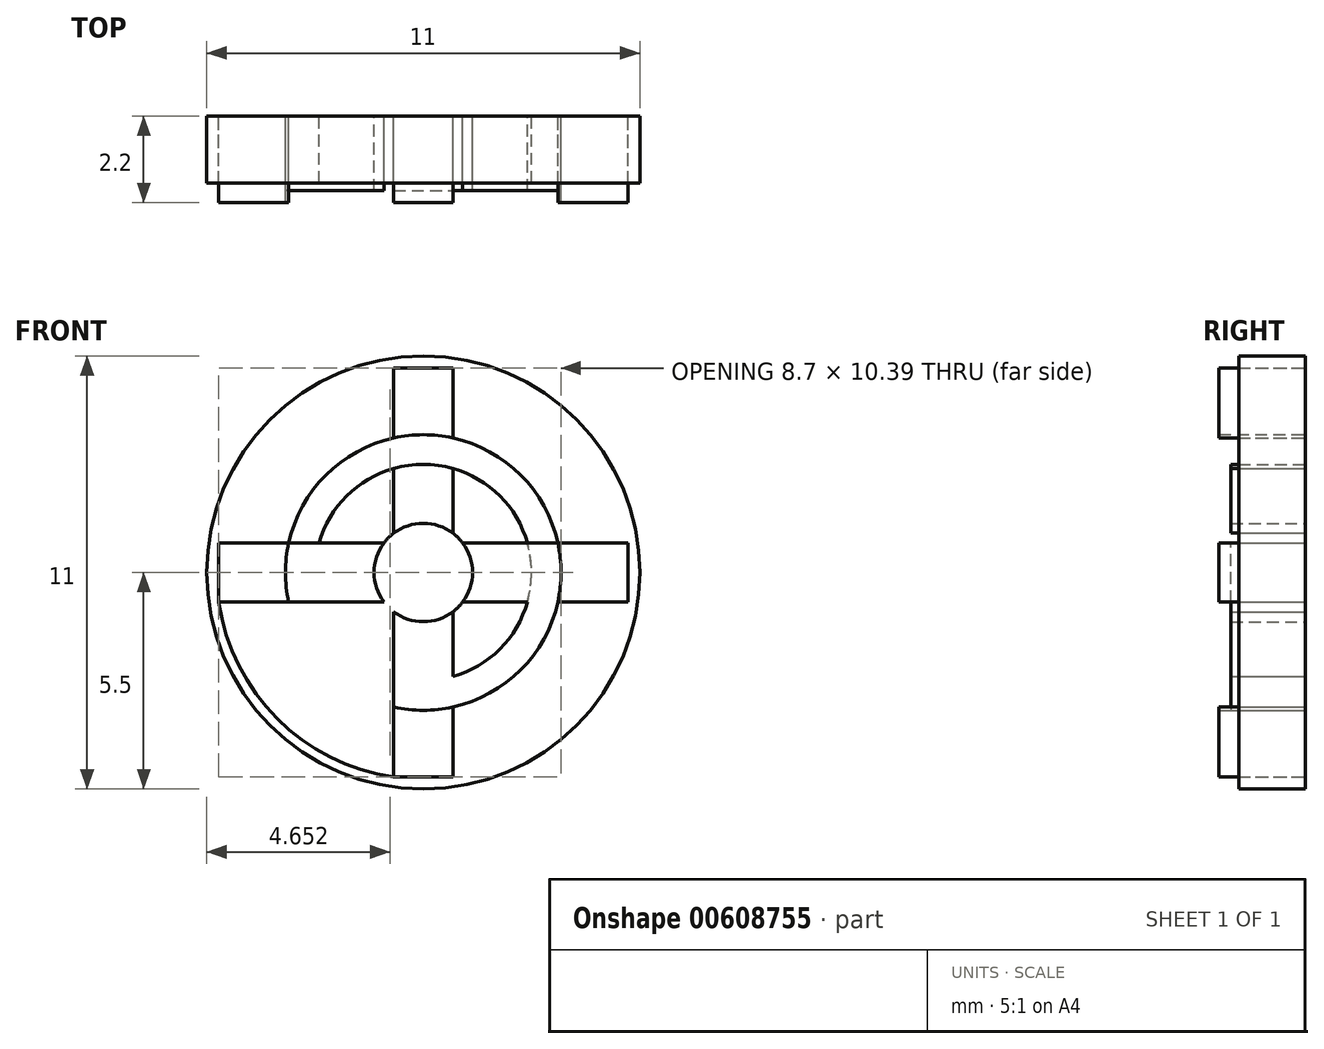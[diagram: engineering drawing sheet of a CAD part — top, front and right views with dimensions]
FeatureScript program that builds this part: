
annotation { "Feature Type Name" : "Feature", "Feature Type Description" : "" }
export const myFeature = defineFeature(function(context is Context, id is Id, definition is map)
    precondition{}
    {
        {
            var Q0;
            Q0=qCreatedBy(makeId("Front.planeOp"),FACE);
            var sketch = newSketch(context, id + "F0", { "sketchPlane" : qUnion([Q0])});
            skCircle(sketch, "E0", {"center": v(0, 0) * mm, "radius": 5.5 * mm});
            skCircle(sketch, "E1", {"center": v(0, 0) * mm, "radius": 1.25 * mm});
            skCircle(sketch, "E2", {"center": v(0, 0) * mm, "radius": 2.75 * mm});
            skCircle(sketch, "E3", {"center": v(0, 0) * mm, "radius": 3.5 * mm});
            skCircle(sketch, "E4", {"center": v(0, 0) * mm, "radius": 5.25 * mm});
            skLineSegment(sketch, "E5.bottom", {"start": v(-5.2, -0.75) * mm, "end": v(5.2, -0.75) * mm});
            skLineSegment(sketch, "E5.top", {"start": v(-5.2, 0.75) * mm, "end": v(5.2, 0.75) * mm});
            skLineSegment(sketch, "E5.left", {"start": v(-5.2, -0.75) * mm, "end": v(-5.2, 0.75) * mm});
            skLineSegment(sketch, "E5.right", {"start": v(5.2, -0.75) * mm, "end": v(5.2, 0.75) * mm});
            skLineSegment(sketch, "E6.bottom", {"start": v(-0.75, -5.2) * mm, "end": v(0.75, -5.2) * mm});
            skLineSegment(sketch, "E6.top", {"start": v(-0.75, 5.2) * mm, "end": v(0.75, 5.2) * mm});
            skLineSegment(sketch, "E6.left", {"start": v(-0.75, -5.2) * mm, "end": v(-0.75, 5.2) * mm});
            skLineSegment(sketch, "E6.right", {"start": v(0.75, -5.2) * mm, "end": v(0.75, 5.2) * mm});
            skSolve(sketch);
        }
        {
            var Q0;
            {var subQ0=sQuery(id+"F0.wireOp",EDGE,"E6.right");var subQ1=sQuery(id+"F0.wireOp",EDGE,"E1");var subQ2=makeQuery(id+"F0.imprint","INTERSECT",VERTEX,{"disambiguationData":[OD(0.0)],"derivedFrom":[subQ1,subQ0]});Q0=makeQuery(id+"F0.imprint","IMPRINT",FACE,{"disambiguationData":[TD([[makeQuery(id+"F0.imprint","IMPRINT",EDGE,{"disambiguationData":[TD([[subQ2,1.0]])],"derivedFrom":subQ1}),-1.0]])]});}
            var Q1;
            {var subQ0=sQuery(id+"F0.wireOp",EDGE,"E6.right");var subQ1=sQuery(id+"F0.wireOp",EDGE,"E3");var subQ2=makeQuery(id+"F0.imprint","INTERSECT",VERTEX,{"disambiguationData":[OD(0.0)],"derivedFrom":[subQ1,subQ0]});Q1=makeQuery(id+"F0.imprint","IMPRINT",FACE,{"disambiguationData":[TD([[makeQuery(id+"F0.imprint","IMPRINT",EDGE,{"disambiguationData":[TD([[subQ2,1.0]])],"derivedFrom":subQ1}),-1.0]])]});}
            var Q2;
            {var subQ0=sQuery(id+"F0.wireOp",EDGE,"E6.left");var subQ1=sQuery(id+"F0.wireOp",EDGE,"E1");var subQ2=makeQuery(id+"F0.imprint","INTERSECT",VERTEX,{"disambiguationData":[OD(0.0)],"derivedFrom":[subQ1,subQ0]});Q2=makeQuery(id+"F0.imprint","IMPRINT",FACE,{"disambiguationData":[TD([[makeQuery(id+"F0.imprint","IMPRINT",EDGE,{"disambiguationData":[TD([[subQ2,-1.0]])],"derivedFrom":subQ1}),-1.0]])]});}
            var Q3;
            Q3=makeQuery(id+"F0.imprint","IMPRINT",FACE,{"disambiguationData":[TD([[makeQuery(id+"F0.imprint","IMPRINT",EDGE,{"derivedFrom":sQuery(id+"F0.wireOp",EDGE,"E0")}),1.0]])]});
            var Q4;
            {var subQ0=sQuery(id+"F0.wireOp",EDGE,"E5.bottom");var subQ1=sQuery(id+"F0.wireOp",EDGE,"E3");var subQ2=makeQuery(id+"F0.imprint","INTERSECT",VERTEX,{"disambiguationData":[OD(0.0)],"derivedFrom":[subQ1,subQ0]});Q4=makeQuery(id+"F0.imprint","IMPRINT",FACE,{"disambiguationData":[TD([[makeQuery(id+"F0.imprint","IMPRINT",EDGE,{"disambiguationData":[TD([[subQ2,-1.0]])],"derivedFrom":subQ1}),-1.0]])]});}
            var Q5;
            {var subQ0=sQuery(id+"F0.wireOp",EDGE,"E5.bottom");var subQ1=sQuery(id+"F0.wireOp",EDGE,"E1");var subQ2=makeQuery(id+"F0.imprint","INTERSECT",VERTEX,{"disambiguationData":[OD(0.0)],"derivedFrom":[subQ1,subQ0]});Q5=makeQuery(id+"F0.imprint","IMPRINT",FACE,{"disambiguationData":[TD([[makeQuery(id+"F0.imprint","IMPRINT",EDGE,{"disambiguationData":[TD([[subQ2,-1.0]])],"derivedFrom":subQ1}),-1.0]])]});}
            var Q6;
            {var subQ0=sQuery(id+"F0.wireOp",EDGE,"E6.left");var subQ1=sQuery(id+"F0.wireOp",EDGE,"E3");var subQ2=makeQuery(id+"F0.imprint","INTERSECT",VERTEX,{"disambiguationData":[OD(0.0)],"derivedFrom":[subQ1,subQ0]});Q6=makeQuery(id+"F0.imprint","IMPRINT",FACE,{"disambiguationData":[TD([[makeQuery(id+"F0.imprint","IMPRINT",EDGE,{"disambiguationData":[TD([[subQ2,-1.0]])],"derivedFrom":subQ1}),-1.0]])]});}
            var Q7;
            {var subQ0=sQuery(id+"F0.wireOp",EDGE,"E6.right");var subQ1=sQuery(id+"F0.wireOp",EDGE,"E1");var subQ2=makeQuery(id+"F0.imprint","INTERSECT",VERTEX,{"disambiguationData":[OD(1.0)],"derivedFrom":[subQ1,subQ0]});Q7=makeQuery(id+"F0.imprint","IMPRINT",FACE,{"disambiguationData":[TD([[makeQuery(id+"F0.imprint","IMPRINT",EDGE,{"disambiguationData":[TD([[subQ2,-1.0]])],"derivedFrom":subQ1}),-1.0]])]});}
            var Q8;
            {var subQ0=sQuery(id+"F0.wireOp",EDGE,"E6.right");var subQ1=sQuery(id+"F0.wireOp",EDGE,"E3");var subQ2=makeQuery(id+"F0.imprint","INTERSECT",VERTEX,{"disambiguationData":[OD(1.0)],"derivedFrom":[subQ1,subQ0]});Q8=makeQuery(id+"F0.imprint","IMPRINT",FACE,{"disambiguationData":[TD([[makeQuery(id+"F0.imprint","IMPRINT",EDGE,{"disambiguationData":[TD([[subQ2,-1.0]])],"derivedFrom":subQ1}),-1.0]])]});}
            var Q9;
            {var subQ0=sQuery(id+"F0.wireOp",EDGE,"E6.top");Q9=makeQuery(id+"F0.imprint","IMPRINT",FACE,{"disambiguationData":[TD([[makeQuery(id+"F0.imprint","IMPRINT",EDGE,{"derivedFrom":subQ0}),1.0]])]});}
            var Q10;
            {var subQ0=sQuery(id+"F0.wireOp",EDGE,"E6.bottom");Q10=makeQuery(id+"F0.imprint","IMPRINT",FACE,{"disambiguationData":[TD([[makeQuery(id+"F0.imprint","IMPRINT",EDGE,{"derivedFrom":subQ0}),-1.0]])]});}
            var Q11;
            {var subQ0=sQuery(id+"F0.wireOp",EDGE,"E5.right");Q11=makeQuery(id+"F0.imprint","IMPRINT",FACE,{"disambiguationData":[TD([[makeQuery(id+"F0.imprint","IMPRINT",EDGE,{"derivedFrom":subQ0}),-1.0]])]});}
            var Q12;
            {var subQ0=sQuery(id+"F0.wireOp",EDGE,"E5.left");Q12=makeQuery(id+"F0.imprint","IMPRINT",FACE,{"disambiguationData":[TD([[makeQuery(id+"F0.imprint","IMPRINT",EDGE,{"derivedFrom":subQ0}),1.0]])]});}
            extrude(context, id + "F1", {"entities" : qUnion([Q0, Q1, Q2, Q3, Q4, Q5, Q6, Q7, Q8, Q9, Q10, Q11, Q12]), "depth" : 1.7 * mm, "offsetDistance" : 25 * mm});
        }
        {
            var Q0;
            {var subQ0=sQuery(id+"F0.wireOp",EDGE,"E5.top");var subQ1=sQuery(id+"F0.wireOp",EDGE,"E2");var subQ2=makeQuery(id+"F0.imprint","INTERSECT",VERTEX,{"disambiguationData":[OD(1.0)],"derivedFrom":[subQ1,subQ0]});Q0=makeQuery(id+"F0.imprint","IMPRINT",FACE,{"disambiguationData":[TD([[makeQuery(id+"F0.imprint","IMPRINT",EDGE,{"disambiguationData":[TD([[subQ2,-1.0]])],"derivedFrom":subQ1}),-1.0]])]});}
            var Q1;
            {var subQ0=sQuery(id+"F0.wireOp",EDGE,"E5.top");var subQ1=sQuery(id+"F0.wireOp",EDGE,"E1");var subQ2=makeQuery(id+"F0.imprint","INTERSECT",VERTEX,{"disambiguationData":[OD(1.0)],"derivedFrom":[subQ1,subQ0]});Q1=makeQuery(id+"F0.imprint","IMPRINT",FACE,{"disambiguationData":[TD([[makeQuery(id+"F0.imprint","IMPRINT",EDGE,{"disambiguationData":[TD([[subQ2,-1.0]])],"derivedFrom":subQ1}),-1.0]])]});}
            var Q2;
            {var subQ0=sQuery(id+"F0.wireOp",EDGE,"E6.right");var subQ1=sQuery(id+"F0.wireOp",EDGE,"E1");var subQ2=makeQuery(id+"F0.imprint","INTERSECT",VERTEX,{"disambiguationData":[OD(0.0)],"derivedFrom":[subQ1,subQ0]});Q2=makeQuery(id+"F0.imprint","IMPRINT",FACE,{"disambiguationData":[TD([[makeQuery(id+"F0.imprint","IMPRINT",EDGE,{"disambiguationData":[TD([[subQ2,-1.0]])],"derivedFrom":subQ1}),-1.0]])]});}
            var Q3;
            {var subQ0=sQuery(id+"F0.wireOp",EDGE,"E6.right");var subQ1=sQuery(id+"F0.wireOp",EDGE,"E2");var subQ2=makeQuery(id+"F0.imprint","INTERSECT",VERTEX,{"disambiguationData":[OD(0.0)],"derivedFrom":[subQ1,subQ0]});Q3=makeQuery(id+"F0.imprint","IMPRINT",FACE,{"disambiguationData":[TD([[makeQuery(id+"F0.imprint","IMPRINT",EDGE,{"disambiguationData":[TD([[subQ2,-1.0]])],"derivedFrom":subQ1}),-1.0]])]});}
            var Q4;
            {var subQ0=sQuery(id+"F0.wireOp",EDGE,"E5.top");var subQ1=sQuery(id+"F0.wireOp",EDGE,"E2");var subQ2=makeQuery(id+"F0.imprint","INTERSECT",VERTEX,{"disambiguationData":[OD(0.0)],"derivedFrom":[subQ1,subQ0]});Q4=makeQuery(id+"F0.imprint","IMPRINT",FACE,{"disambiguationData":[TD([[makeQuery(id+"F0.imprint","IMPRINT",EDGE,{"disambiguationData":[TD([[subQ2,1.0]])],"derivedFrom":subQ1}),-1.0]])]});}
            var Q5;
            {var subQ0=sQuery(id+"F0.wireOp",EDGE,"E5.top");var subQ1=sQuery(id+"F0.wireOp",EDGE,"E1");var subQ2=makeQuery(id+"F0.imprint","INTERSECT",VERTEX,{"disambiguationData":[OD(0.0)],"derivedFrom":[subQ1,subQ0]});Q5=makeQuery(id+"F0.imprint","IMPRINT",FACE,{"disambiguationData":[TD([[makeQuery(id+"F0.imprint","IMPRINT",EDGE,{"disambiguationData":[TD([[subQ2,1.0]])],"derivedFrom":subQ1}),-1.0]])]});}
            var Q6;
            {var subQ0=sQuery(id+"F0.wireOp",EDGE,"E6.left");var subQ1=sQuery(id+"F0.wireOp",EDGE,"E2");var subQ2=makeQuery(id+"F0.imprint","INTERSECT",VERTEX,{"disambiguationData":[OD(1.0)],"derivedFrom":[subQ1,subQ0]});Q6=makeQuery(id+"F0.imprint","IMPRINT",FACE,{"disambiguationData":[TD([[makeQuery(id+"F0.imprint","IMPRINT",EDGE,{"disambiguationData":[TD([[subQ2,-1.0]])],"derivedFrom":subQ1}),-1.0]])]});}
            var Q7;
            {var subQ0=sQuery(id+"F0.wireOp",EDGE,"E6.left");var subQ1=sQuery(id+"F0.wireOp",EDGE,"E1");var subQ2=makeQuery(id+"F0.imprint","INTERSECT",VERTEX,{"disambiguationData":[OD(1.0)],"derivedFrom":[subQ1,subQ0]});Q7=makeQuery(id+"F0.imprint","IMPRINT",FACE,{"disambiguationData":[TD([[makeQuery(id+"F0.imprint","IMPRINT",EDGE,{"disambiguationData":[TD([[subQ2,-1.0]])],"derivedFrom":subQ1}),-1.0]])]});}
            extrude(context, id + "F2", {"entities" : qUnion([Q0, Q1, Q2, Q3, Q4, Q5, Q6, Q7]), "depth" : 1.9 * mm, "offsetDistance" : 25 * mm});
        }
        {
            var Q0;
            {var subQ5=sQuery(id+"F0.wireOp",EDGE,"E5.left");Q0=makeQuery(id+"F0.imprint","IMPRINT",FACE,{"disambiguationData":[TD([[makeQuery(id+"F0.imprint","IMPRINT",EDGE,{"derivedFrom":subQ5}),-1.0]])]});}
            var Q1;
            {var subQ5=sQuery(id+"F0.wireOp",EDGE,"E6.top");Q1=makeQuery(id+"F0.imprint","IMPRINT",FACE,{"disambiguationData":[TD([[makeQuery(id+"F0.imprint","IMPRINT",EDGE,{"derivedFrom":subQ5}),-1.0]])]});}
            var Q2;
            {var subQ5=sQuery(id+"F0.wireOp",EDGE,"E5.right");Q2=makeQuery(id+"F0.imprint","IMPRINT",FACE,{"disambiguationData":[TD([[makeQuery(id+"F0.imprint","IMPRINT",EDGE,{"derivedFrom":subQ5}),1.0]])]});}
            var Q3;
            {var subQ5=sQuery(id+"F0.wireOp",EDGE,"E6.bottom");Q3=makeQuery(id+"F0.imprint","IMPRINT",FACE,{"disambiguationData":[TD([[makeQuery(id+"F0.imprint","IMPRINT",EDGE,{"derivedFrom":subQ5}),1.0]])]});}
            extrude(context, id + "F3", {"entities" : qUnion([Q0, Q1, Q2, Q3]), "depth" : 2.2 * mm, "offsetDistance" : 25 * mm});
        }
    });
